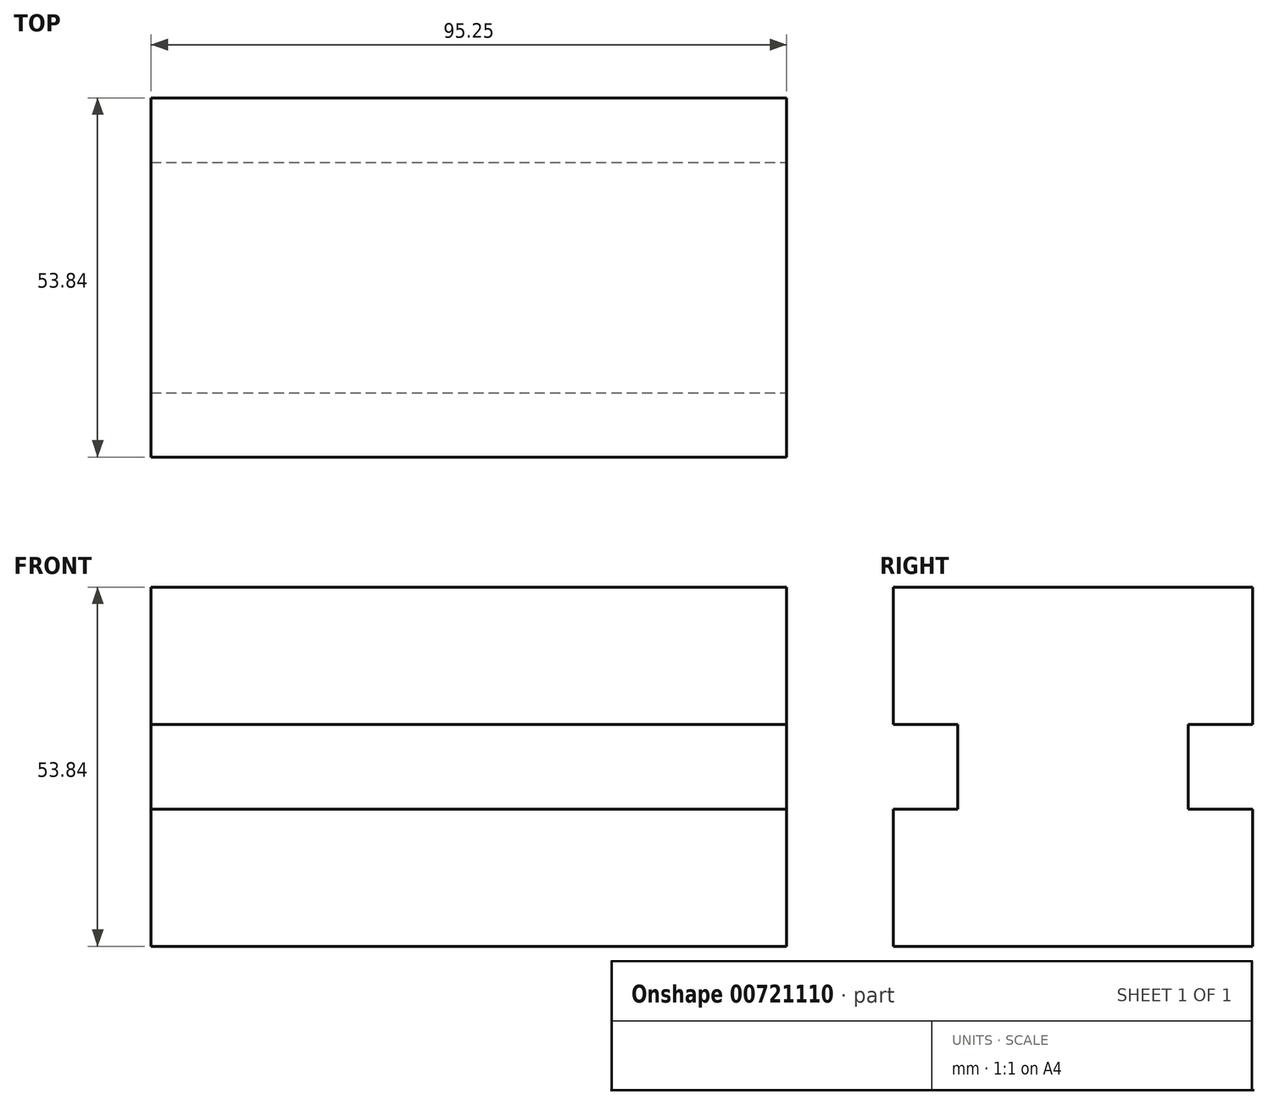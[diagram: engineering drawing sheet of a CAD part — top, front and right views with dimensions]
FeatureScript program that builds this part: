
annotation { "Feature Type Name" : "Feature", "Feature Type Description" : "" }
export const myFeature = defineFeature(function(context is Context, id is Id, definition is map)
    precondition{}
    {
        {
            var Q0;
            Q0=qCreatedBy(makeId("Right.planeOp"),FACE);
            var sketch = newSketch(context, id + "F0", { "sketchPlane" : qUnion([Q0])});
            skLineSegment(sketch, "E0.bottom", {"start": v(26.92, -26.92) * mm, "end": v(-26.92, -26.92) * mm});
            skLineSegment(sketch, "E0.top", {"start": v(26.92, 26.92) * mm, "end": v(-26.92, 26.92) * mm});
            skLineSegment(sketch, "E0.left", {"start": v(26.92, -26.92) * mm, "end": v(26.92, -6.35) * mm});
            skLineSegment(sketch, "E0.right", {"start": v(-26.92, -26.92) * mm, "end": v(-26.92, -6.35) * mm});
            skPoint(sketch, "E0.middle", {"position": v(0, 0) * mm});
            skLineSegment(sketch, "E1.bottom", {"start": v(-26.92, 6.35) * mm, "end": v(-17.27, 6.35) * mm});
            skLineSegment(sketch, "E1.top", {"start": v(-26.92, -6.35) * mm, "end": v(-17.27, -6.35) * mm});
            skLineSegment(sketch, "E1.right", {"start": v(-17.27, 6.35) * mm, "end": v(-17.27, -6.35) * mm});
            skLineSegment(sketch, "E2", {"start": v(0, 38.87) * mm, "end": v(0, -47.8) * mm, "construction": true});
            skLineSegment(sketch, "E3.MirrorCS", {"start": v(17.27, 6.35) * mm, "end": v(17.27, -6.35) * mm});
            skLineSegment(sketch, "E4.MirrorCS", {"start": v(26.92, 6.35) * mm, "end": v(17.27, 6.35) * mm});
            skLineSegment(sketch, "E5.MirrorCS", {"start": v(26.92, -6.35) * mm, "end": v(17.27, -6.35) * mm});
            skLineSegment(sketch, "E6.trimOffspring", {"start": v(-26.92, 6.35) * mm, "end": v(-26.92, 26.92) * mm});
            skLineSegment(sketch, "E7.trimOffspring", {"start": v(26.92, 6.35) * mm, "end": v(26.92, 26.92) * mm});
            skSolve(sketch);
        }
        {
            var Q0;
            Q0=makeQuery(id+"F0.imprint","IMPRINT",FACE,{"disambiguationData":[TD([[makeQuery(id+"F0.imprint","IMPRINT",EDGE,{"derivedFrom":sQuery(id+"F0.wireOp",EDGE,"E0.bottom")}),-1.0]])]});
            extrude(context, id + "F1", {"entities" : qUnion([Q0]), "oppositeDirection" : true, "depth" : 95.25 * mm, "offsetDistance" : 25.4 * mm});
        }
    });
